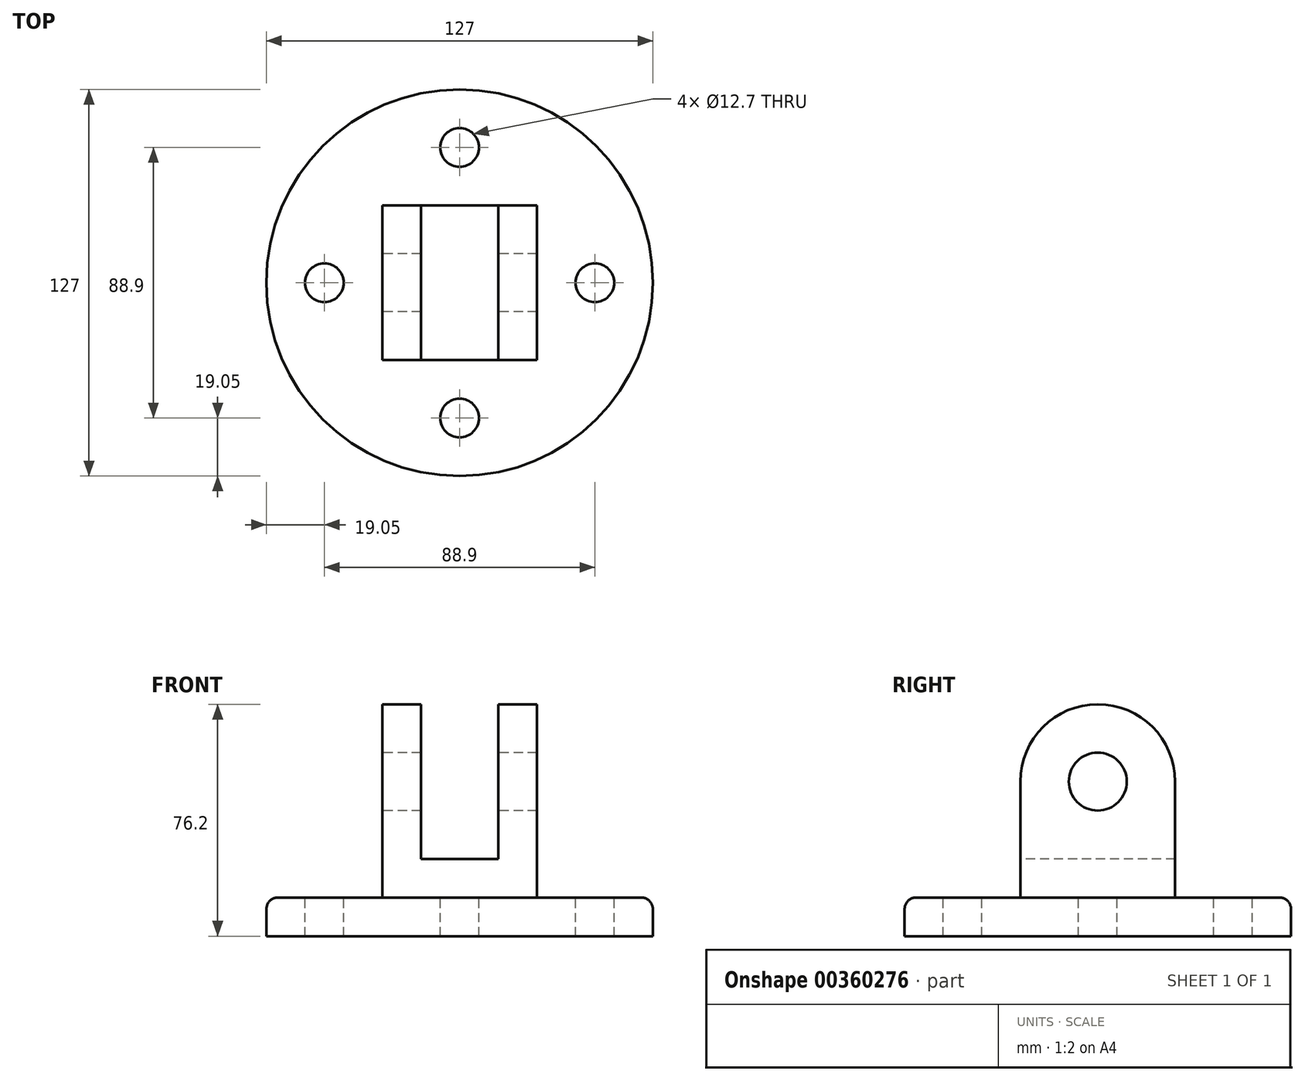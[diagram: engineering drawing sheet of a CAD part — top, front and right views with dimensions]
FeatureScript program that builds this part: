
annotation { "Feature Type Name" : "Feature", "Feature Type Description" : "" }
export const myFeature = defineFeature(function(context is Context, id is Id, definition is map)
    precondition{}
    {
        {
            var Q0;
            Q0=qCreatedBy(makeId("Top.planeOp"),FACE);
            var sketch = newSketch(context, id + "F0", { "sketchPlane" : qUnion([Q0])});
            skCircle(sketch, "E0", {"center": v(0, 0) * mm, "radius": 63.5 * mm});
            skCircle(sketch, "E1", {"center": v(0, 0) * mm, "radius": 44.45 * mm, "construction": true});
            skLineSegment(sketch, "E2", {"start": v(-71.71, 0) * mm, "end": v(77.95, 0) * mm, "construction": true});
            skLineSegment(sketch, "E3", {"start": v(0, 70.62) * mm, "end": v(0, -76.23) * mm, "construction": true});
            skCircle(sketch, "E4", {"center": v(0, 44.45) * mm, "radius": 6.35 * mm});
            skCircle(sketch, "E5", {"center": v(44.45, 0) * mm, "radius": 6.35 * mm});
            skCircle(sketch, "E6", {"center": v(0, -44.45) * mm, "radius": 6.35 * mm});
            skCircle(sketch, "E7", {"center": v(-44.45, 0) * mm, "radius": 6.35 * mm});
            skSolve(sketch);
        }
        {
            var Q0;
            Q0 = qSketchRegion(id + "F0", true);
            extrude(context, id + "F1", {"entities" : qUnion([Q0]), "oppositeDirection" : true, "depth" : 12.7 * mm});
        }
        {
            var Q0;
            Q0=qCreatedBy(makeId("Right.planeOp"),FACE);
            var sketch = newSketch(context, id + "F2", { "sketchPlane" : qUnion([Q0])});
            skLineSegment(sketch, "E8.bottom", {"start": v(25.4, 0) * mm, "end": v(-25.4, 0) * mm});
            skLineSegment(sketch, "E8.top", {"start": v(25.4, 38.1) * mm, "end": v(-25.4, 38.1) * mm});
            skLineSegment(sketch, "E8.left", {"start": v(25.4, 0) * mm, "end": v(25.4, 38.1) * mm});
            skLineSegment(sketch, "E8.right", {"start": v(-25.4, 0) * mm, "end": v(-25.4, 38.1) * mm});
            skArc(sketch, "E9", {"start": v(-25.4, 38.1) * mm, "mid": v(0, 63.5) * mm, "end": v(25.4, 38.1) * mm});
            skCircle(sketch, "E10", {"center": v(0, 38.1) * mm, "radius": 9.53 * mm});
            skSolve(sketch);
        }
        {
            var Q0;
            Q0 = qSketchRegion(id + "F2", true);
            extrude(context, id + "F3", {"entities" : qUnion([Q0]), "operationType" : NewBodyOperationType.ADD, "endBound" : BoundingType.SYMMETRIC, "depth" : 50.8 * mm});
        }
        {
            var Q0;
            Q0=qCreatedBy(makeId("Front.planeOp"),FACE);
            var sketch = newSketch(context, id + "F4", { "sketchPlane" : qUnion([Q0])});
            skLineSegment(sketch, "E11.bottom", {"start": v(-12.7, 12.7) * mm, "end": v(12.7, 12.7) * mm});
            skLineSegment(sketch, "E11.top", {"start": v(-12.7, 95.85) * mm, "end": v(12.7, 95.85) * mm});
            skLineSegment(sketch, "E11.left", {"start": v(-12.7, 12.7) * mm, "end": v(-12.7, 95.85) * mm});
            skLineSegment(sketch, "E11.right", {"start": v(12.7, 12.7) * mm, "end": v(12.7, 95.85) * mm});
            skSolve(sketch);
        }
        {
            var Q0;
            Q0 = qSketchRegion(id + "F4", true);
            extrude(context, id + "F5", {"entities" : qUnion([Q0]), "operationType" : NewBodyOperationType.REMOVE, "endBound" : BoundingType.THROUGH_ALL, "oppositeDirection" : true, "depth" : 25.4 * mm, "hasSecondDirection" : true, "secondDirectionBound" : SecondDirectionBoundingType.THROUGH_ALL, "secondDirectionOppositeDirection" : false, "secondDirectionDepth" : 25.4 * mm});
        }
        {
            var Q0;
            Q0=makeQuery(id+"F1.opExtrude","CAP_EDGE",EDGE,{"disambiguationData":[OSD([sQuery(id+"F0.wireOp",EDGE,"E0")])],"isStart":true});
            var Q1;
            Q1=makeQuery(id+"F3.opExtrude","SWEPT_EDGE",EDGE,{"disambiguationData":[OSD([sQuery(id+"F2.wireOp",EDGE,"E8.bottom"),sQuery(id+"F2.wireOp",EDGE,"E8.right")])]});
            var Q2;
            Q2=makeQuery(id+"F3.opExtrude","CAP_EDGE",EDGE,{"disambiguationData":[OSD([sQuery(id+"F2.wireOp",EDGE,"E8.bottom")])],"isStart":false});
            var Q3;
            Q3=makeQuery(id+"F3.opExtrude","SWEPT_EDGE",EDGE,{"disambiguationData":[OSD([sQuery(id+"F2.wireOp",EDGE,"E8.bottom"),sQuery(id+"F2.wireOp",EDGE,"E8.left")])]});
            var Q4;
            Q4=makeQuery(id+"F3.opExtrude","CAP_EDGE",EDGE,{"disambiguationData":[OSD([sQuery(id+"F2.wireOp",EDGE,"E8.bottom")])],"isStart":true});
            fillet(context, id + "F6", {"entities" : qUnion([Q0, Q1, Q2, Q3, Q4]), "radius" : 3.8 * mm, "tangentPropagation" : true, "allowEdgeOverflow" : false});
        }
    });
